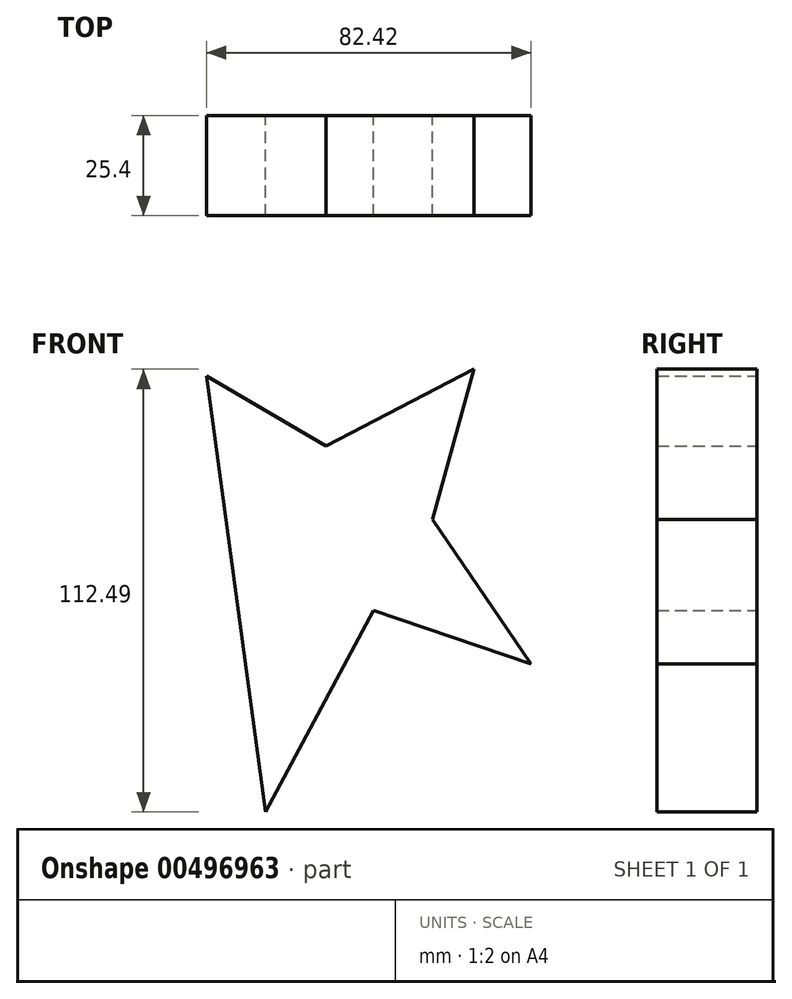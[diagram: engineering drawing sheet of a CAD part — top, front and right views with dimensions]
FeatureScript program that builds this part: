
annotation { "Feature Type Name" : "Feature", "Feature Type Description" : "" }
export const myFeature = defineFeature(function(context is Context, id is Id, definition is map)
    precondition{}
    {
        {
            var Q0;
            Q0=qCreatedBy(makeId("Front.planeOp"),FACE);
            var sketch = newSketch(context, id + "F0", { "sketchPlane" : qUnion([Q0])});
            skLineSegment(sketch, "E0", {"start": v(0, -51.13) * mm, "end": v(27.37, 0) * mm});
            skLineSegment(sketch, "E1", {"start": v(27.37, 0) * mm, "end": v(67.38, -13.54) * mm});
            skLineSegment(sketch, "E2", {"start": v(67.38, -13.54) * mm, "end": v(42.41, 23.16) * mm});
            skLineSegment(sketch, "E3", {"start": v(42.41, 23.16) * mm, "end": v(52.94, 61.36) * mm});
            skLineSegment(sketch, "E4", {"start": v(52.94, 61.36) * mm, "end": v(15.34, 41.8) * mm});
            skLineSegment(sketch, "E5", {"start": v(15.34, 41.8) * mm, "end": v(-15.04, 59.56) * mm});
            skLineSegment(sketch, "E6", {"start": v(-15.04, 59.56) * mm, "end": v(0, -51.13) * mm});
            skSolve(sketch);
        }
        {
            var Q0;
            Q0=makeQuery(id+"F0.imprint","IMPRINT",FACE,{"disambiguationData":[TD([[makeQuery(id+"F0.imprint","IMPRINT",EDGE,{"derivedFrom":sQuery(id+"F0.wireOp",EDGE,"E0")}),1.0]])]});
            extrude(context, id + "F1", {"entities" : qUnion([Q0]), "depth" : 25.4 * mm});
        }
    });
